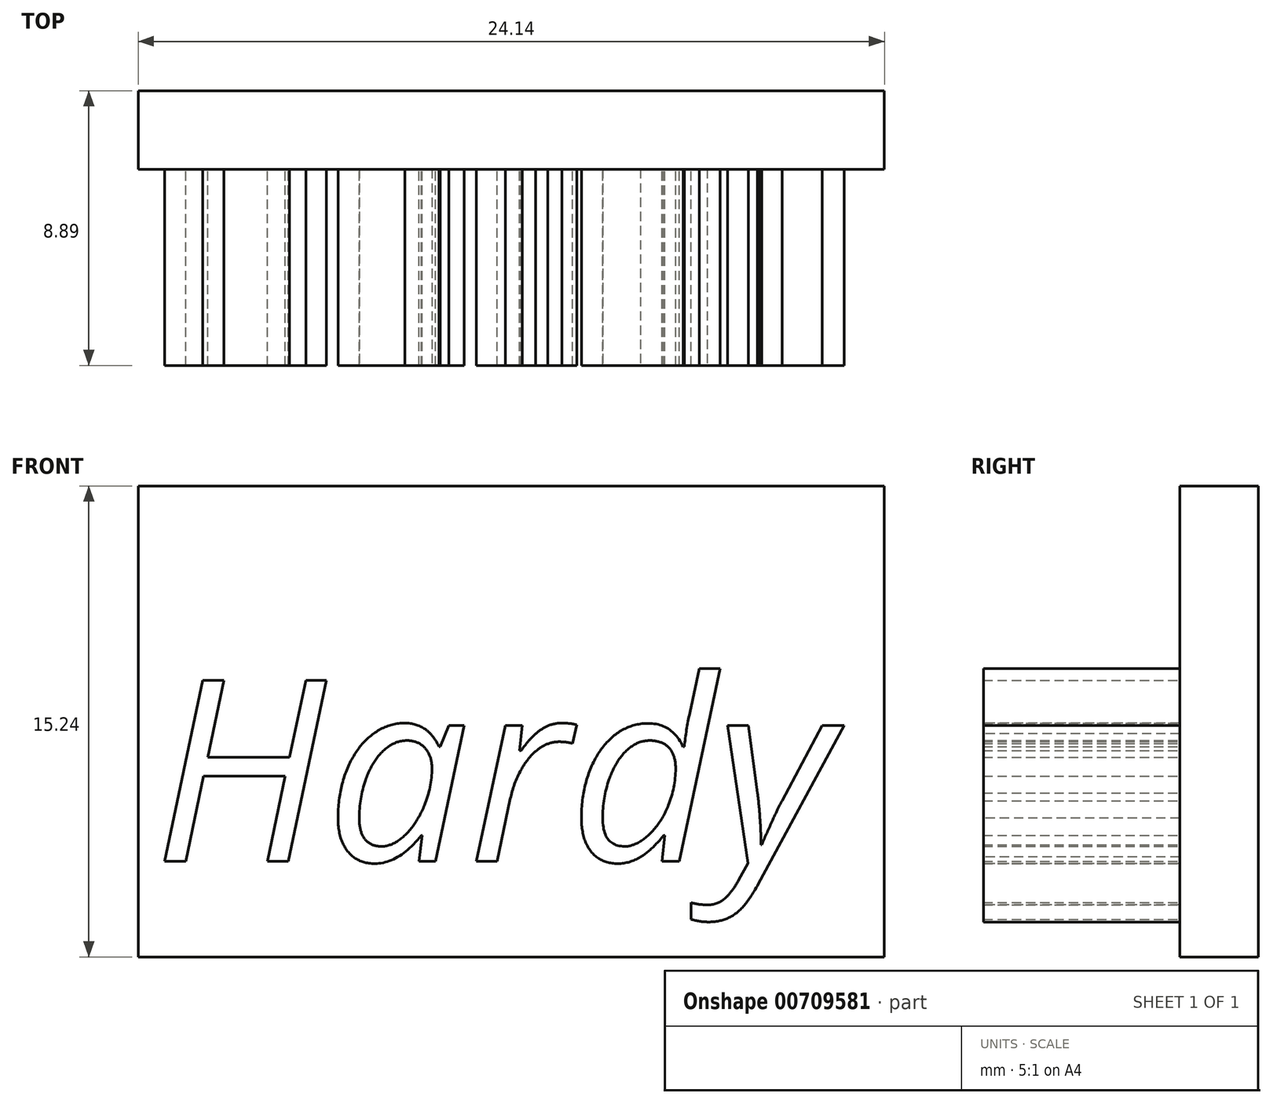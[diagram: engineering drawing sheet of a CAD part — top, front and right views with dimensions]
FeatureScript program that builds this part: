
annotation { "Feature Type Name" : "Feature", "Feature Type Description" : "" }
export const myFeature = defineFeature(function(context is Context, id is Id, definition is map)
    precondition{}
    {
        {
            var Q0;
            Q0=qCreatedBy(makeId("Front.planeOp"),FACE);
            var sketch = newSketch(context, id + "F0", { "sketchPlane" : qUnion([Q0])});
            skLineSegment(sketch, "E0.bottom", {"start": v(-12.06, 7.62) * mm, "end": v(12.07, 7.62) * mm});
            skLineSegment(sketch, "E0.top", {"start": v(-12.07, -7.62) * mm, "end": v(12.07, -7.62) * mm});
            skLineSegment(sketch, "E0.left", {"start": v(-12.06, 7.62) * mm, "end": v(-12.07, -7.62) * mm});
            skLineSegment(sketch, "E0.right", {"start": v(12.07, 7.62) * mm, "end": v(12.07, -7.62) * mm});
            skPoint(sketch, "E0.middle", {"position": v(0, 0) * mm});
            skSolve(sketch);
        }
        {
            var Q0;
            Q0=makeQuery(id+"F0.imprint","IMPRINT",FACE,{"disambiguationData":[TD([[makeQuery(id+"F0.imprint","IMPRINT",EDGE,{"derivedFrom":sQuery(id+"F0.wireOp",EDGE,"E0.bottom")}),-1.0]])]});
            extrude(context, id + "F1", {"entities" : qUnion([Q0]), "depth" : 2.54 * mm, "offsetDistance" : 25.4 * mm});
        }
        {
            var Q0;
            Q0=makeQuery(id+"F1.opExtrude","CAP_FACE",FACE,{"disambiguationData":[OSD([sQuery(id+"F0.wireOp",EDGE,"E0.bottom"),sQuery(id+"F0.wireOp",EDGE,"E0.top"),sQuery(id+"F0.wireOp",EDGE,"E0.left"),sQuery(id+"F0.wireOp",EDGE,"E0.right")])],"isStart":false});
            var sketch = newSketch(context, id + "F2", { "sketchPlane" : qUnion([Q0])});
            skText(sketch, "E1", { "text": "Hardy", "fontName": "OpenSans-Italic.ttf"});
            const initialGuessF2  = {"E1": [-0.01156, -0.00452, 1, 0, 0.0059]};
            skSetInitialGuess(sketch, initialGuessF2);
            skSolve(sketch);
        }
        {
            var Q0;
            Q0 = qSketchRegion(id + "F2", true);
            extrude(context, id + "F3", {"entities" : qUnion([Q0]), "operationType" : NewBodyOperationType.ADD, "depth" : 6.35 * mm, "offsetDistance" : 25.4 * mm});
        }
    });
